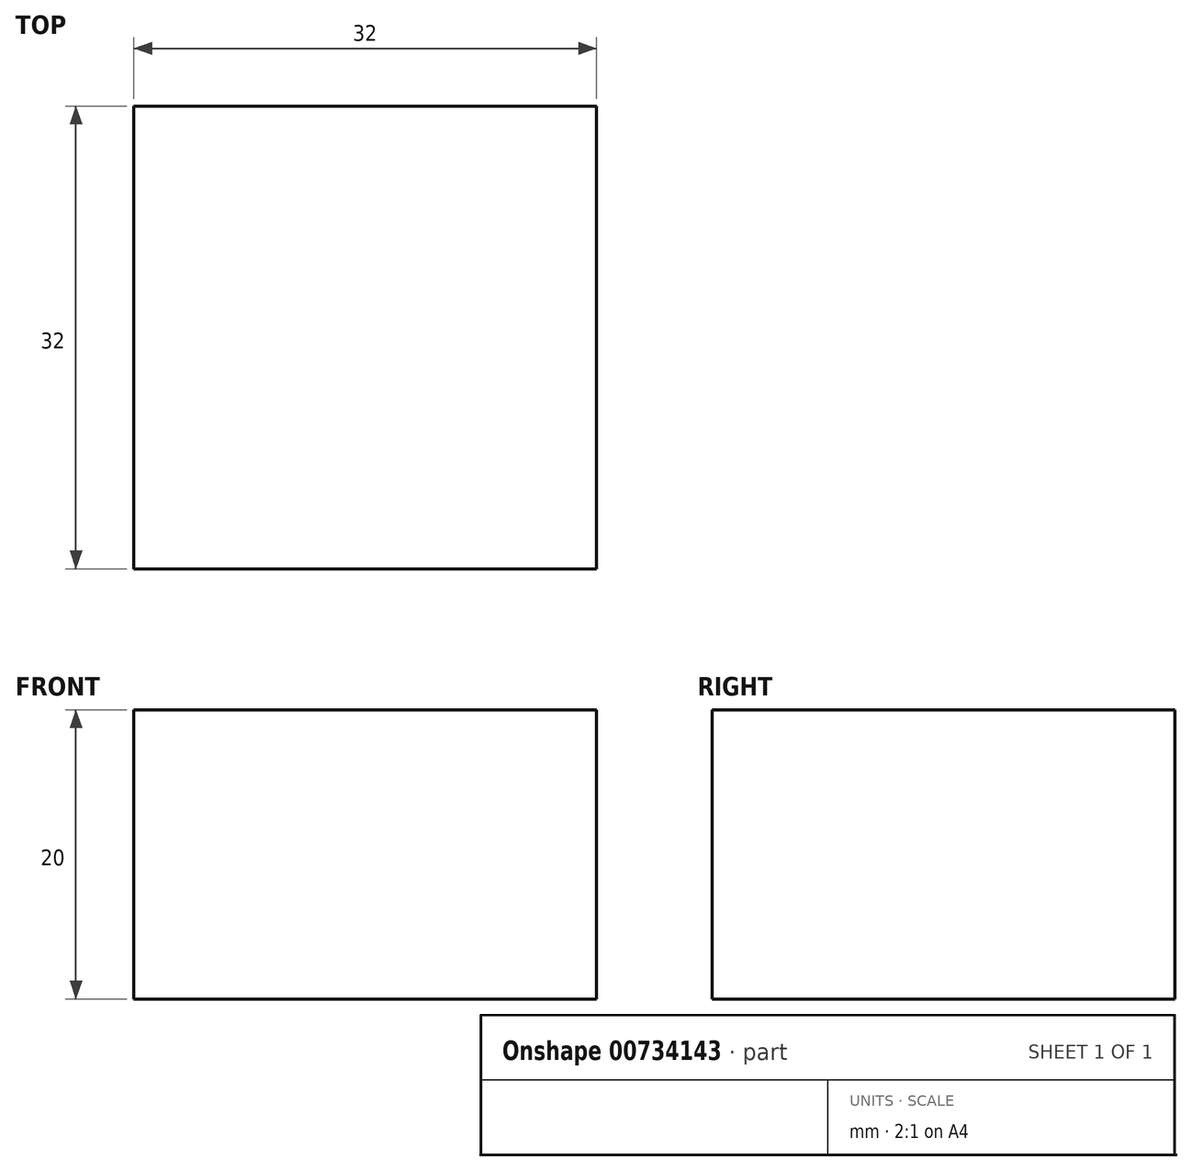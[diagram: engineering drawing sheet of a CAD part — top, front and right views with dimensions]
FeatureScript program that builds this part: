
annotation { "Feature Type Name" : "Feature", "Feature Type Description" : "" }
export const myFeature = defineFeature(function(context is Context, id is Id, definition is map)
    precondition{}
    {
        {
            var Q0;
            Q0=qCreatedBy(makeId("Top.planeOp"),FACE);
            var sketch = newSketch(context, id + "F0", { "sketchPlane" : qUnion([Q0])});
            skLineSegment(sketch, "E0.bottom", {"start": v(-26.59, -23.97) * mm, "end": v(5.41, -23.97) * mm});
            skLineSegment(sketch, "E0.top", {"start": v(-26.59, -55.97) * mm, "end": v(5.41, -55.97) * mm});
            skLineSegment(sketch, "E0.left", {"start": v(-26.59, -23.97) * mm, "end": v(-26.59, -55.97) * mm});
            skLineSegment(sketch, "E0.right", {"start": v(5.41, -23.97) * mm, "end": v(5.41, -55.97) * mm});
            skSolve(sketch);
        }
        {
            var Q0;
            Q0=makeQuery(id+"F0.imprint","IMPRINT",FACE,{"disambiguationData":[TD([[makeQuery(id+"F0.imprint","IMPRINT",EDGE,{"derivedFrom":sQuery(id+"F0.wireOp",EDGE,"E0.bottom")}),-1.0]])]});
            extrude(context, id + "F1", {"entities" : qUnion([Q0]), "depth" : 20 * mm, "offsetDistance" : 25 * mm});
        }
    });
